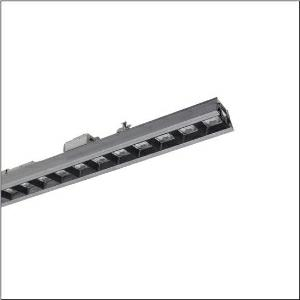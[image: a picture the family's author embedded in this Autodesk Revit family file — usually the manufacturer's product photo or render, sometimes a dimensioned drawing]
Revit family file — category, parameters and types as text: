
# Revit family: licross_r__21_silica_51ts12dn4zm00583xx_641b
name_source: partatom
category: Lighting Fixtures
units: mm (PartAtom-declared; Revit-internal decimal feet)

## family parameters
Cut with Voids When Loaded = No
Host = Face
Light Source = No
Part Type = Normal
Room Calculation Point = No
Round Connector Dimension = Use Diameter
Shared = No

## types (1)
- --- (1 x LED, 6340 lm, 39 W, 4000K)
    Apparent Load = 39 VA
    CIE Flux Codes = 86 100 100 100 100
    Color Rendering = 80
    Color Temperature = 4000K
    Default Elevation = 1800 mm
    Description = Licross® 21 Silica, luminaire insert, of sheet steel, galvanised, coil coated, silver, length: 1.500mm, width: 82mm, height: 86mm, LED rated luminous flux: 6.340lm, light colour: 840, control gear: DALI 2, with plug, 5-pole, with phase selection, mains connection: 220..240V, AC, 50/60Hz, rated input power: 39W, internal wiring halogen-free, primary light control with lens, of PMMA, primary anti-glare with darklight reflector, of PC, CAT 2 (L<= 1000cd/m²), light emission: direct distribution, primary light characteristic: symmetric, protection rating (complete): IP40, insulation class (complete): insulation class I (protective earthing), certification: CE, UKCA, protection symbol: D if used in an environment without relevant dust loads, impact resistance: IK03, permissible ambient temperature for indoor applications: -25..+45°C, corresponds to IFS (International Featured Standards) requirements for safety and quality in the food industry, reducing of maximum allowable ambient temperature of 5°C with ceiling mounting, LABS conformity tested according to VDMA 24364:2018-05, packaging unit: 1 piece
    Height = 86 mm
    Lamp = 1 x LED
    Lamp Light Flux = 6340 lm
    Lamp Power = 39 W
    Lamp count = 1
    Length = 1500 mm
    Luminous efficacy = 163 lm/W
    Manufacturer = Siteco
    ModVariant = No
    Model = 51TS12DN4ZM00583XX
    Mounting Place = Ceiling
    Mounting Type = Pendant
    Number of Poles = 1
    OnlyDefault = Yes
    Power Factor = 1
    Product Name = Licross® 21 Silica
    Product group = luminaire insert | ceiling pendant
    ProductGroupID = 902
    Protection Class = Protection class I
    Protection Degree = IP 40
    RLX_Detail_Level = 1
    RLX_Emergency_Light_Flux = 0 lm
    RLX_Emergency_Type = 0
    RLX_Emergency_Type_DB = No
    RlxData = <blob elided: 56945 chars, md5=3ca99185>
    Socket = socket
    Standby Power = 0 W
    System Light Flux = 6340 lm
    System Power = 39 W
    Type Comments = factory setting: luminous flux: 100 % | dim-lin: 254 | 435 mA
    Type Image = l_1290833.jpg
    URL = http://relux.com
    VarID = @adj_127827
    Voltage = 0 V
    Weight = 0.00 kg
    Width = 82 mm  [stored 0.269029 ft]

note: [stored X ft] marks values corroborated as IEEE doubles in the binary element streams (Revit-internal decimal feet)

## geometry (parser evidence)
native form markers: Blend x4, Sweep x13
no freeform markers — native parametric forms only
